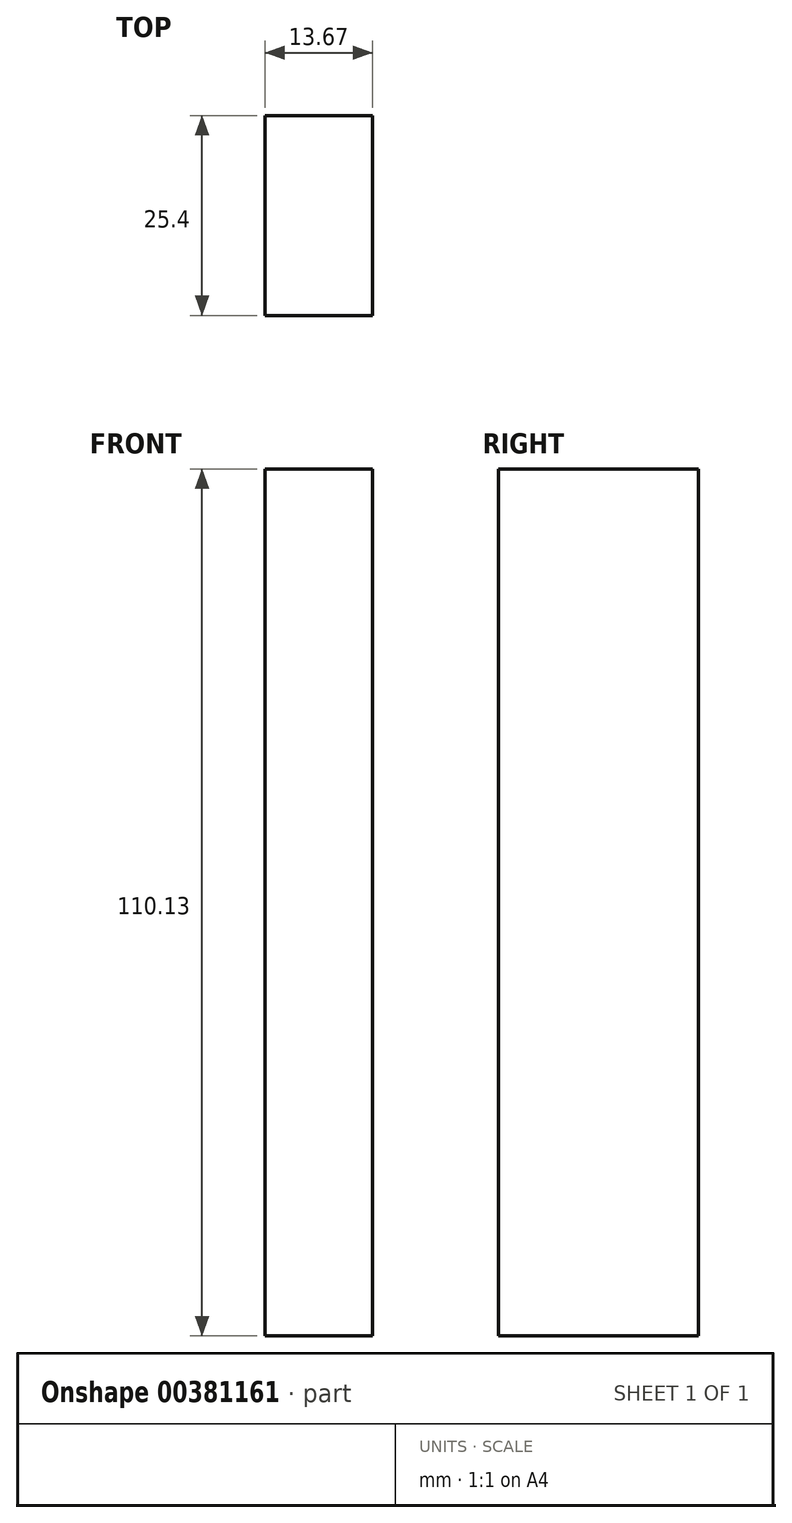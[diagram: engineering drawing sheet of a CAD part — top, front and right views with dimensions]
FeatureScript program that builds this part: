
annotation { "Feature Type Name" : "Feature", "Feature Type Description" : "" }
export const myFeature = defineFeature(function(context is Context, id is Id, definition is map)
    precondition{}
    {
        {
            var Q0;
            Q0=qCreatedBy(makeId("Front.planeOp"),FACE);
            var sketch = newSketch(context, id + "F0", { "sketchPlane" : qUnion([Q0])});
            skLineSegment(sketch, "E0.bottom", {"start": v(0, 23.28) * mm, "end": v(0, 23.28) * mm});
            skLineSegment(sketch, "E0.top", {"start": v(0, 59.87) * mm, "end": v(0, 59.87) * mm});
            skLineSegment(sketch, "E0.left", {"start": v(0, 23.28) * mm, "end": v(0, 59.87) * mm});
            skLineSegment(sketch, "E0.right", {"start": v(0, 23.28) * mm, "end": v(0, 59.87) * mm});
            skLineSegment(sketch, "E1.bottom", {"start": v(0, -50.26) * mm, "end": v(13.67, -50.26) * mm});
            skLineSegment(sketch, "E1.top", {"start": v(0, 59.87) * mm, "end": v(13.67, 59.87) * mm});
            skLineSegment(sketch, "E1.left", {"start": v(0, -50.26) * mm, "end": v(0, 59.87) * mm});
            skLineSegment(sketch, "E1.right", {"start": v(13.67, -50.26) * mm, "end": v(13.67, 59.87) * mm});
            skSolve(sketch);
        }
        {
            var Q0;
            {var subQ0=sQuery(id+"F0.wireOp",EDGE,"E1.bottom");Q0=makeQuery(id+"F0.imprint","IMPRINT",FACE,{"disambiguationData":[TD([[makeQuery(id+"F0.imprint","IMPRINT",EDGE,{"derivedFrom":subQ0}),1.0]])]});}
            extrude(context, id + "F1", {"entities" : qUnion([Q0]), "depth" : 25.4 * mm});
        }
    });
